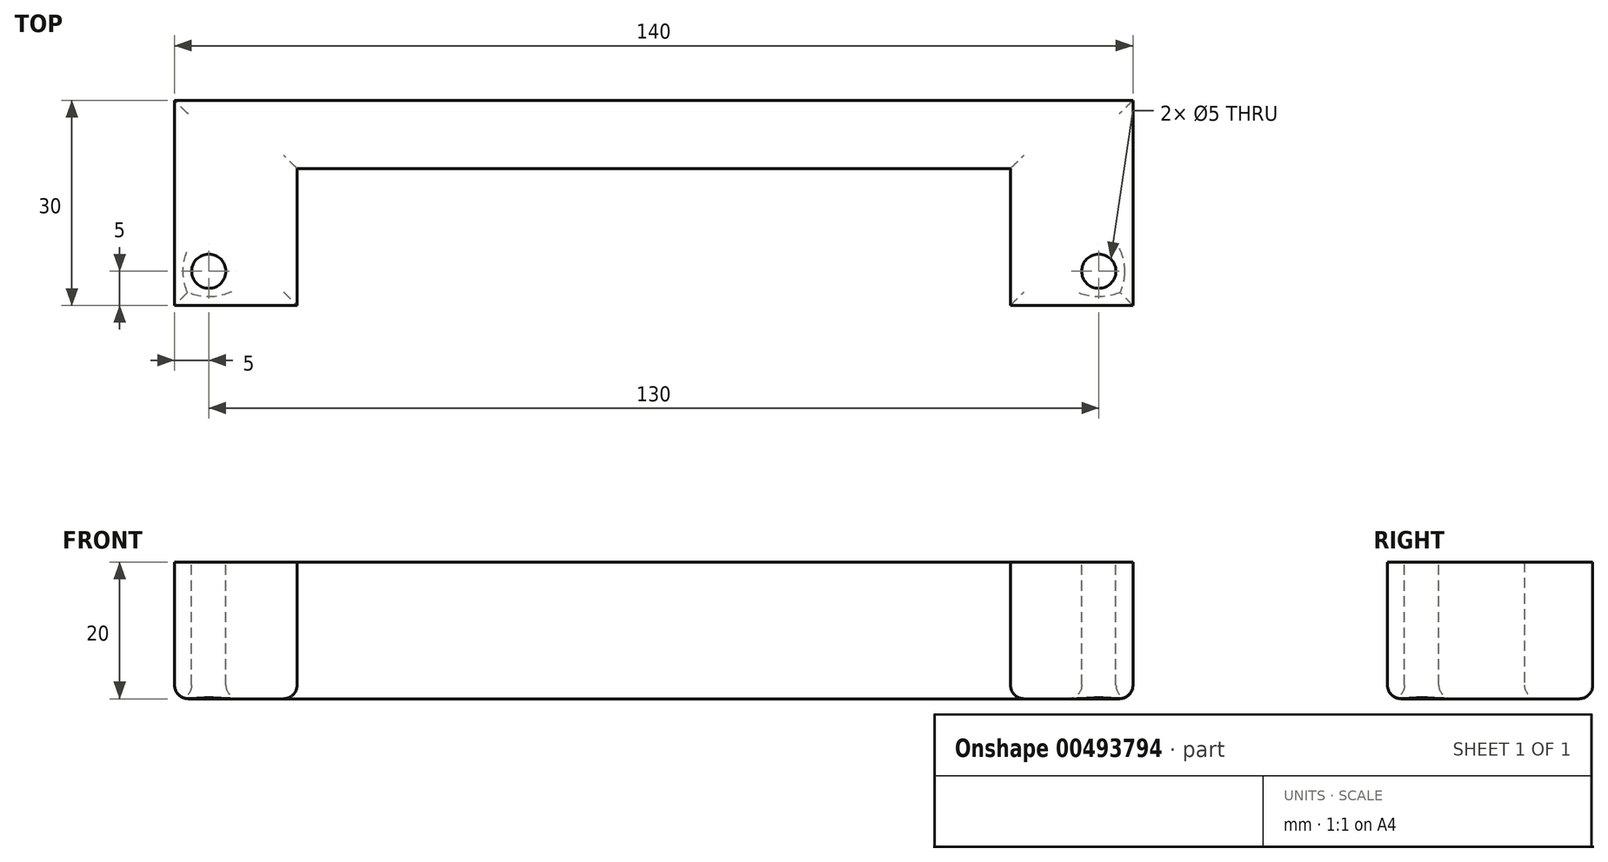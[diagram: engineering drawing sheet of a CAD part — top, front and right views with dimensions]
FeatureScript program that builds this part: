
annotation { "Feature Type Name" : "Feature", "Feature Type Description" : "" }
export const myFeature = defineFeature(function(context is Context, id is Id, definition is map)
    precondition{}
    {
        {
            var Q0;
            Q0=qCreatedBy(makeId("Top.planeOp"),FACE);
            var sketch = newSketch(context, id + "F0", { "sketchPlane" : qUnion([Q0])});
            skLineSegment(sketch, "E0", {"start": v(0, 30) * mm, "end": v(0, 20) * mm});
            skLineSegment(sketch, "E1", {"start": v(0, 20) * mm, "end": v(52.1, 20) * mm});
            skLineSegment(sketch, "E2", {"start": v(52.1, 20) * mm, "end": v(52.1, 0) * mm});
            skLineSegment(sketch, "E3", {"start": v(52.1, 0) * mm, "end": v(70, 0) * mm});
            skLineSegment(sketch, "E4", {"start": v(70, 0) * mm, "end": v(70, 30) * mm});
            skLineSegment(sketch, "E5", {"start": v(0, 30) * mm, "end": v(70, 30) * mm});
            skSolve(sketch);
        }
        {
            var Q0;
            Q0=makeQuery(id+"F0.imprint","IMPRINT",FACE,{"disambiguationData":[TD([[makeQuery(id+"F0.imprint","IMPRINT",EDGE,{"derivedFrom":sQuery(id+"F0.wireOp",EDGE,"E0")}),1.0]])]});
            extrude(context, id + "F1", {"entities" : qUnion([Q0]), "depth" : 20 * mm});
        }
        {
            var Q0;
            Q0=makeQuery(id+"F1.opExtrude","CAP_FACE",FACE,{"disambiguationData":[OSD([sQuery(id+"F0.wireOp",EDGE,"E0"),sQuery(id+"F0.wireOp",EDGE,"E1"),sQuery(id+"F0.wireOp",EDGE,"E2"),sQuery(id+"F0.wireOp",EDGE,"E3"),sQuery(id+"F0.wireOp",EDGE,"E4"),sQuery(id+"F0.wireOp",EDGE,"E5")])],"isStart":false});
            var sketch = newSketch(context, id + "F2", { "sketchPlane" : qUnion([Q0])});
            skPoint(sketch, "E6", {"position": v(65, 5) * mm});
            skSolve(sketch);
        }
        {
            var Q0;
            Q0=sQuery(id+"F2.wireOp",VERTEX,"E6");
            var Q1;
            Q1=makeQuery(id+"F1.opExtrude","SWEPT_BODY",BODY,{"disambiguationData":[OSD([sQuery(id+"F0.wireOp",EDGE,"E0"),sQuery(id+"F0.wireOp",EDGE,"E1"),sQuery(id+"F0.wireOp",EDGE,"E2"),sQuery(id+"F0.wireOp",EDGE,"E3"),sQuery(id+"F0.wireOp",EDGE,"E4"),sQuery(id+"F0.wireOp",EDGE,"E5")])]});
            hole(context, id + "F3", {"style" : HoleStyle.SIMPLE, "endStyle" : HoleEndStyle.THROUGH, "holeDiameter" : 5 * mm, "isTappedThrough" : true, "tappedDepth" : 12 * mm, "tapClearance" : 3, "locations" : qUnion([Q0]), "scope" : qUnion([Q1])});
        }
        {
            var Q0;
            Q0=makeQuery(id+"F1.opExtrude","SWEPT_BODY",BODY,{"disambiguationData":[OSD([sQuery(id+"F0.wireOp",EDGE,"E0"),sQuery(id+"F0.wireOp",EDGE,"E1"),sQuery(id+"F0.wireOp",EDGE,"E2"),sQuery(id+"F0.wireOp",EDGE,"E3"),sQuery(id+"F0.wireOp",EDGE,"E4"),sQuery(id+"F0.wireOp",EDGE,"E5")])]});
            var Q1;
            Q1=makeQuery(id+"F1.opExtrude","SWEPT_FACE",FACE,{"disambiguationData":[OSD([sQuery(id+"F0.wireOp",EDGE,"E0")])]});
            mirror(context, id + "F4", {"operationType" : NewBodyOperationType.ADD, "entities" : qUnion([Q0]), "mirrorPlane" : qUnion([Q1])});
        }
        {
            var Q0;
            {var subQ0=makeQuery(id+"F1.opExtrude","CAP_FACE",FACE,{"disambiguationData":[OSD([sQuery(id+"F0.wireOp",EDGE,"E0"),sQuery(id+"F0.wireOp",EDGE,"E1"),sQuery(id+"F0.wireOp",EDGE,"E2"),sQuery(id+"F0.wireOp",EDGE,"E3"),sQuery(id+"F0.wireOp",EDGE,"E4"),sQuery(id+"F0.wireOp",EDGE,"E5")])],"isStart":true});Q0=makeQuery(id+"F4.boolean.opBoolean","MERGE",FACE,{"derivedFrom":[subQ0,makeQuery(id+"F4.opPattern","COPY",FACE,{"derivedFrom":subQ0,"instanceName":"1"})]});}
            fillet(context, id + "F5", {"entities" : qUnion([Q0]), "radius" : 2 * mm, "tangentPropagation" : true, "allowEdgeOverflow" : false});
        }
    });
